# Revit family: K1-SB
name_source: partatom
category: Modèles génériques
units: mm (PartAtom-declared; Revit-internal decimal feet)

## family parameters
Basée sur le plan de construction = Oui
Cote de connecteur circulaire = Utiliser le diamètre
Couper avec des vides une fois chargée = Non
Numéro OmniClass = 23.85.10.11.14.14.14
Partagée = Non
Peut héberger une armature = Non
Point de calcul de pièce = Non
Titre OmniClass = Loudspeakers
Toujours verticalement = Non
Type d'élément = Normal

## types (1)
- K1-SB
    Amplified by = LA12X
    Cabinet = Baltic birch plywood
    Connectors = IN: 1 x 4 point SpeakON
    Description = SUBWOOFER ENCLOSURE
    Elévation par défaut = 0 mm  [stored 0 ft]
    Fabricant = L-Acoustics
    Finish standard = L-Acoustics - Dark Grey Brown (Pantone 426C)
    IP rating = IP55
    Low frequency limit (-10 dB) = 30 Hz ([K1SB_60])
    Maximal SPL = 145 dB ([K1SB_X])
    Modèle = K1-SB
    Nominal impedance = 4 Ω
    Transducers = 2 x 15''   |   4'' coil
    URL = https://www.l-acoustics.com
    Version = v1.0.0

note: [stored X ft] marks values corroborated as IEEE doubles in the binary element streams (Revit-internal decimal feet)
